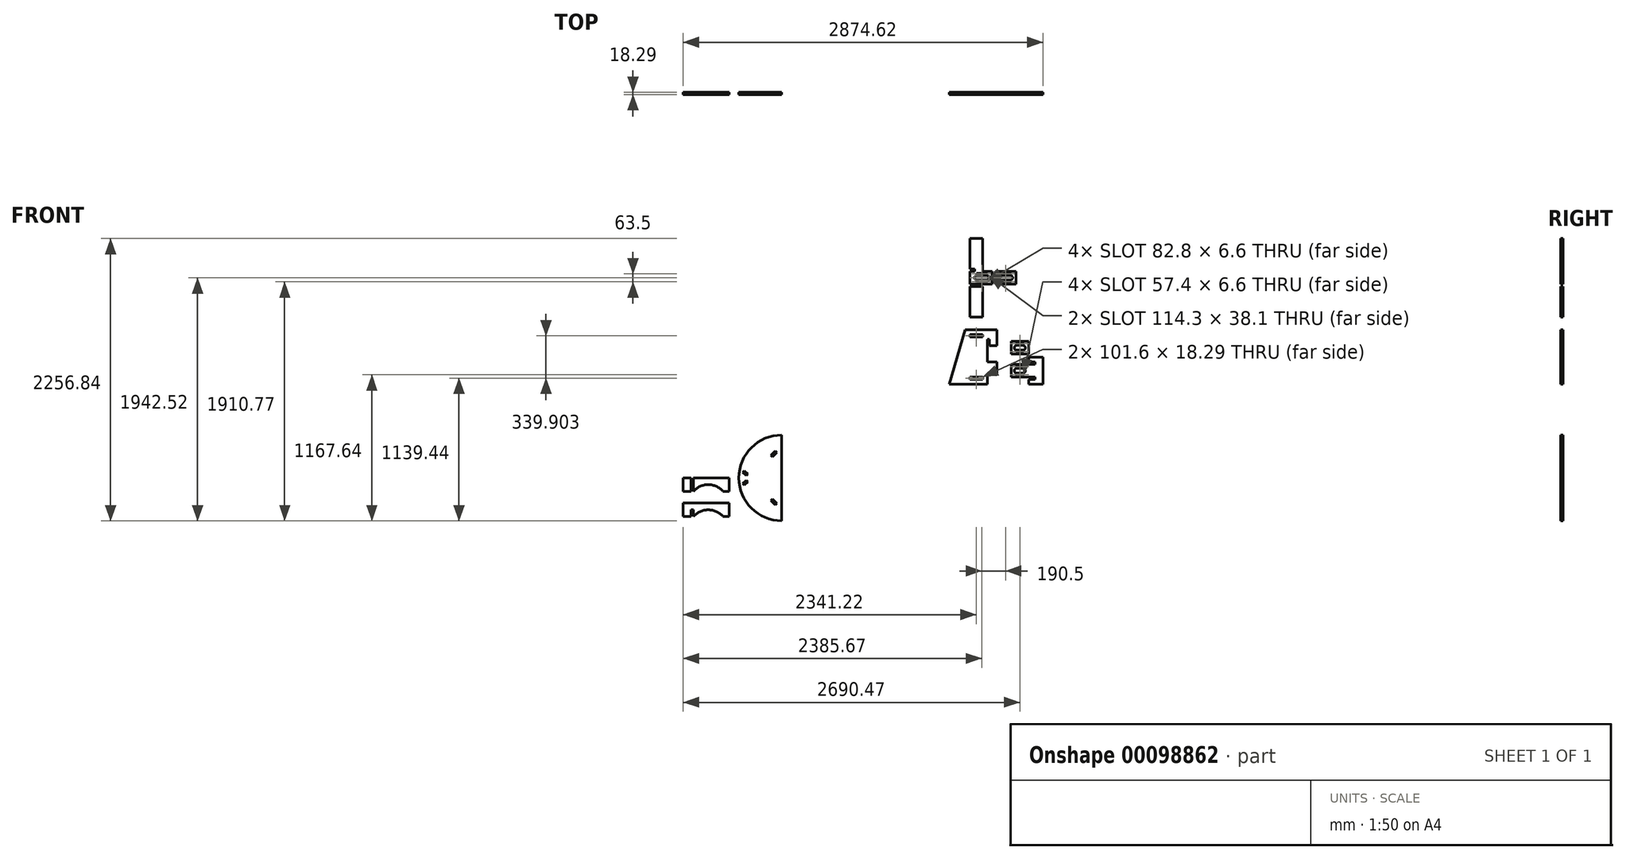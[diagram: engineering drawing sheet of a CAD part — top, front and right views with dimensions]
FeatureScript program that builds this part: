
annotation { "Feature Type Name" : "Feature", "Feature Type Description" : "" }
export const myFeature = defineFeature(function(context is Context, id is Id, definition is map)
    precondition{}
    {
        {
            var Q0;
            Q0=qCreatedBy(makeId("Front.planeOp"),FACE);
            var sketch = newSketch(context, id + "F0", { "sketchPlane" : qUnion([Q0])});
            skLineSegment(sketch, "E0.bottom", {"start": v(-889, 508) * mm, "end": v(889, 508) * mm, "construction": true});
            skLineSegment(sketch, "E0.top", {"start": v(-889, -508) * mm, "end": v(889, -508) * mm, "construction": true});
            skLineSegment(sketch, "E0.left", {"start": v(-889, 508) * mm, "end": v(-889, -508) * mm, "construction": true});
            skLineSegment(sketch, "E0.right", {"start": v(889, 508) * mm, "end": v(889, -508) * mm, "construction": true});
            skPoint(sketch, "E0.middle", {"position": v(0, 0) * mm});
            skArc(sketch, "E1", {"start": v(-889, 177.8) * mm, "mid": v(-1231.9, -165.1) * mm, "end": v(-889, -508) * mm, "construction": true});
            skLineSegment(sketch, "E2", {"start": v(0, -508) * mm, "end": v(0, 508) * mm, "construction": true});
            skArc(sketch, "E3", {"start": v(-1651, 177.8) * mm, "mid": v(-1993.9, -165.1) * mm, "end": v(-1651, -508) * mm});
            skLineSegment(sketch, "E4", {"start": v(-1651, 177.8) * mm, "end": v(-1651, -508) * mm});
            skPoint(sketch, "E5.startSnap0", {"position": v(-1993.9, -165.1) * mm});
            skLineSegment(sketch, "E6", {"start": v(-1689.1, 38.1) * mm, "end": v(-1689.1, -368.3) * mm});
            skLineSegment(sketch, "E7.0", {"start": v(-1981.97, -254.77) * mm, "end": v(-1689.1, 38.1) * mm, "construction": true});
            skLineSegment(sketch, "E8.0", {"start": v(-1981.97, -75.43) * mm, "end": v(-1689.1, -368.3) * mm, "construction": true});
            skLineSegment(sketch, "E9.0", {"start": v(-1986.93, -96.33) * mm, "end": v(-1689.1, -394.16) * mm, "construction": true});
            skLineSegment(sketch, "E10.0", {"start": v(-1986.93, -233.87) * mm, "end": v(-1689.1, 63.96) * mm, "construction": true});
            skPoint(sketch, "E11", {"position": v(-1918.16, -165.1) * mm});
            skLineSegment(sketch, "E12", {"start": v(-1993.9, -165.1) * mm, "end": v(-1651, -165.1) * mm, "construction": true});
            skPoint(sketch, "E13", {"position": v(-1689.1, -165.1) * mm});
            skLineSegment(sketch, "E14", {"start": v(-1963.06, -120.2) * mm, "end": v(-1950.13, -107.27) * mm});
            skLineSegment(sketch, "E15", {"start": v(-1936.12, -147.14) * mm, "end": v(-1923.2, -134.2) * mm});
            skLineSegment(sketch, "E16", {"start": v(-1689.1, -368.3) * mm, "end": v(-1702.03, -381.23) * mm});
            skLineSegment(sketch, "E17", {"start": v(-1725.02, -332.38) * mm, "end": v(-1737.95, -345.31) * mm});
            skLineSegment(sketch, "E18", {"start": v(-1950.13, -107.27) * mm, "end": v(-1923.2, -134.2) * mm});
            skLineSegment(sketch, "E19", {"start": v(-1936.12, -147.14) * mm, "end": v(-1963.06, -120.2) * mm});
            skLineSegment(sketch, "E20", {"start": v(-1737.95, -345.31) * mm, "end": v(-1702.03, -381.23) * mm});
            skLineSegment(sketch, "E21", {"start": v(-1725.02, -332.38) * mm, "end": v(-1689.1, -368.3) * mm});
            skLineSegment(sketch, "E22.MirrorCS", {"start": v(-1689.1, 38.1) * mm, "end": v(-1702.03, 51.03) * mm});
            skLineSegment(sketch, "E23.MirrorCS", {"start": v(-1725.02, 2.18) * mm, "end": v(-1737.95, 15.11) * mm});
            skLineSegment(sketch, "E24.MirrorCS", {"start": v(-1737.95, 15.11) * mm, "end": v(-1702.03, 51.03) * mm});
            skLineSegment(sketch, "E25.MirrorCS", {"start": v(-1725.02, 2.18) * mm, "end": v(-1689.1, 38.1) * mm});
            skLineSegment(sketch, "E26.MirrorCS", {"start": v(-1950.13, -222.93) * mm, "end": v(-1923.2, -196) * mm});
            skLineSegment(sketch, "E27.MirrorCS", {"start": v(-1936.12, -183.06) * mm, "end": v(-1963.06, -210) * mm});
            skLineSegment(sketch, "E28.MirrorCS", {"start": v(-1963.06, -210) * mm, "end": v(-1950.13, -222.93) * mm});
            skLineSegment(sketch, "E29.MirrorCS", {"start": v(-1936.12, -183.06) * mm, "end": v(-1923.2, -196) * mm});
            skLineSegment(sketch, "E30", {"start": v(-1950.13, -107.27) * mm, "end": v(-1689.1, -368.3) * mm});
            skLineSegment(sketch, "E31.bottom", {"start": v(-2439.26, -165.1) * mm, "end": v(-2070.1, -165.1) * mm});
            skLineSegment(sketch, "E31.top", {"start": v(-2439.26, -272.29) * mm, "end": v(-2070.1, -272.29) * mm});
            skLineSegment(sketch, "E31.left", {"start": v(-2439.26, -165.1) * mm, "end": v(-2439.26, -272.29) * mm});
            skLineSegment(sketch, "E31.right", {"start": v(-2070.1, -165.1) * mm, "end": v(-2070.1, -272.29) * mm});
            skLineSegment(sketch, "E32.bottom", {"start": v(-2070.1, -165.1) * mm, "end": v(-2120.9, -165.1) * mm});
            skLineSegment(sketch, "E32.top", {"start": v(-2070.1, -146.81) * mm, "end": v(-2120.9, -146.81) * mm});
            skLineSegment(sketch, "E32.left", {"start": v(-2070.1, -165.1) * mm, "end": v(-2070.1, -146.81) * mm});
            skLineSegment(sketch, "E32.right", {"start": v(-2120.9, -165.1) * mm, "end": v(-2120.9, -146.81) * mm});
            skLineSegment(sketch, "E33.bottom", {"start": v(-2439.26, -165.1) * mm, "end": v(-2401.16, -165.1) * mm});
            skLineSegment(sketch, "E33.top", {"start": v(-2439.26, -146.81) * mm, "end": v(-2401.16, -146.81) * mm});
            skLineSegment(sketch, "E33.left", {"start": v(-2439.26, -165.1) * mm, "end": v(-2439.26, -146.81) * mm});
            skLineSegment(sketch, "E33.right", {"start": v(-2401.16, -165.1) * mm, "end": v(-2401.16, -146.81) * mm});
            skPoint(sketch, "E34.oppositeSnap0", {"position": v(-2439.26, -218.7) * mm});
            skLineSegment(sketch, "E34.bottom", {"start": v(-2375.76, -272.29) * mm, "end": v(-2357.47, -272.29) * mm});
            skLineSegment(sketch, "E34.top", {"start": v(-2375.76, -218.7) * mm, "end": v(-2357.47, -218.7) * mm});
            skLineSegment(sketch, "E34.left", {"start": v(-2375.76, -272.29) * mm, "end": v(-2375.76, -218.7) * mm});
            skLineSegment(sketch, "E34.right", {"start": v(-2357.47, -272.29) * mm, "end": v(-2357.47, -218.7) * mm});
            skLineSegment(sketch, "E35.top", {"start": v(-2375.76, -165.1) * mm, "end": v(-2357.47, -165.1) * mm});
            skLineSegment(sketch, "E35.left", {"start": v(-2375.76, -218.7) * mm, "end": v(-2375.76, -165.1) * mm});
            skLineSegment(sketch, "E35.right", {"start": v(-2357.47, -218.7) * mm, "end": v(-2357.47, -165.1) * mm});
            skLineSegment(sketch, "E36.bottom", {"start": v(-2439.26, -366.78) * mm, "end": v(-2070.1, -366.78) * mm});
            skLineSegment(sketch, "E36.top", {"start": v(-2439.26, -473.96) * mm, "end": v(-2070.1, -473.96) * mm});
            skLineSegment(sketch, "E36.left", {"start": v(-2439.26, -366.78) * mm, "end": v(-2439.26, -473.96) * mm});
            skLineSegment(sketch, "E36.right", {"start": v(-2070.1, -366.78) * mm, "end": v(-2070.1, -473.96) * mm});
            skLineSegment(sketch, "E37.bottom", {"start": v(-2070.1, -366.78) * mm, "end": v(-2120.9, -366.78) * mm});
            skLineSegment(sketch, "E37.top", {"start": v(-2070.1, -348.49) * mm, "end": v(-2120.9, -348.49) * mm});
            skLineSegment(sketch, "E37.left", {"start": v(-2070.1, -366.78) * mm, "end": v(-2070.1, -348.49) * mm});
            skLineSegment(sketch, "E37.right", {"start": v(-2120.9, -366.78) * mm, "end": v(-2120.9, -348.49) * mm});
            skLineSegment(sketch, "E38.bottom", {"start": v(-2439.26, -366.78) * mm, "end": v(-2401.16, -366.78) * mm});
            skLineSegment(sketch, "E38.top", {"start": v(-2439.26, -348.49) * mm, "end": v(-2401.16, -348.49) * mm});
            skLineSegment(sketch, "E38.left", {"start": v(-2439.26, -366.78) * mm, "end": v(-2439.26, -348.49) * mm});
            skLineSegment(sketch, "E38.right", {"start": v(-2401.16, -366.78) * mm, "end": v(-2401.16, -348.49) * mm});
            skPoint(sketch, "E39.oppositeSnap0", {"position": v(-2439.26, -420.37) * mm});
            skLineSegment(sketch, "E39.bottom", {"start": v(-2375.76, -473.96) * mm, "end": v(-2357.47, -473.96) * mm});
            skLineSegment(sketch, "E39.top", {"start": v(-2375.76, -420.37) * mm, "end": v(-2357.47, -420.37) * mm});
            skLineSegment(sketch, "E39.left", {"start": v(-2375.76, -473.96) * mm, "end": v(-2375.76, -420.37) * mm});
            skLineSegment(sketch, "E39.right", {"start": v(-2357.47, -473.96) * mm, "end": v(-2357.47, -420.37) * mm});
            skLineSegment(sketch, "E40.top", {"start": v(-2375.76, -366.78) * mm, "end": v(-2357.47, -366.78) * mm});
            skLineSegment(sketch, "E40.left", {"start": v(-2375.76, -420.37) * mm, "end": v(-2375.76, -366.78) * mm});
            skLineSegment(sketch, "E40.right", {"start": v(-2357.47, -420.37) * mm, "end": v(-2357.47, -366.78) * mm});
            skArc(sketch, "E41", {"start": v(-2120.9, -272.29) * mm, "mid": v(-2239.18, -218.7) * mm, "end": v(-2357.47, -272.29) * mm});
            skLineSegment(sketch, "E42", {"start": v(-2357.47, -218.7) * mm, "end": v(-2070.1, -218.7) * mm, "construction": true});
            skLineSegment(sketch, "E43", {"start": v(-2357.47, -420.37) * mm, "end": v(-2070.1, -420.37) * mm, "construction": true});
            skArc(sketch, "E44", {"start": v(-2120.9, -473.96) * mm, "mid": v(-2239.18, -420.37) * mm, "end": v(-2357.47, -473.96) * mm});
            skLineSegment(sketch, "E45.bottom", {"start": v(9.14, 660.4) * mm, "end": v(-9.14, 660.4) * mm, "construction": true});
            skLineSegment(sketch, "E45.top", {"start": v(9.14, 838.2) * mm, "end": v(-9.14, 838.2) * mm, "construction": true});
            skLineSegment(sketch, "E45.left", {"start": v(9.14, 660.4) * mm, "end": v(9.14, 838.2) * mm, "construction": true});
            skLineSegment(sketch, "E45.right", {"start": v(-9.14, 660.4) * mm, "end": v(-9.14, 838.2) * mm, "construction": true});
            skPoint(sketch, "E45.middle", {"position": v(0, 749.3) * mm});
            skLineSegment(sketch, "E46.bottom", {"start": v(9.14, 942.4) * mm, "end": v(-9.14, 942.4) * mm});
            skLineSegment(sketch, "E46.top", {"start": v(9.14, 929.7) * mm, "end": v(-9.14, 929.7) * mm});
            skLineSegment(sketch, "E46.left", {"start": v(9.14, 942.4) * mm, "end": v(9.14, 929.7) * mm});
            skLineSegment(sketch, "E46.right", {"start": v(-9.14, 942.4) * mm, "end": v(-9.14, 929.7) * mm, "construction": true});
            skPoint(sketch, "E46.middle", {"position": v(0, 936.04) * mm});
            skLineSegment(sketch, "E47.bottom", {"start": v(-9.14, 660.4) * mm, "end": v(67.06, 660.4) * mm});
            skLineSegment(sketch, "E47.top", {"start": v(-9.14, 762) * mm, "end": v(67.06, 762) * mm});
            skLineSegment(sketch, "E47.left", {"start": v(-9.14, 660.4) * mm, "end": v(-9.14, 762) * mm});
            skLineSegment(sketch, "E47.right", {"start": v(67.06, 660.4) * mm, "end": v(67.06, 762) * mm});
            skLineSegment(sketch, "E48.bottom", {"start": v(67.06, 660.4) * mm, "end": v(9.14, 660.4) * mm});
            skLineSegment(sketch, "E48.top", {"start": v(67.06, 584.2) * mm, "end": v(9.14, 584.2) * mm});
            skLineSegment(sketch, "E48.left", {"start": v(67.06, 660.4) * mm, "end": v(67.06, 584.2) * mm});
            skLineSegment(sketch, "E48.right", {"start": v(9.14, 660.4) * mm, "end": v(9.14, 584.2) * mm});
            skLineSegment(sketch, "E49.bottom", {"start": v(-9.14, 929.7) * mm, "end": v(67.06, 929.7) * mm, "construction": true});
            skLineSegment(sketch, "E49.top", {"start": v(-9.14, 1018.6) * mm, "end": v(67.06, 1018.6) * mm});
            skLineSegment(sketch, "E49.left", {"start": v(-9.14, 929.7) * mm, "end": v(-9.14, 1018.6) * mm, "construction": true});
            skLineSegment(sketch, "E49.right", {"start": v(67.06, 929.7) * mm, "end": v(67.06, 1018.6) * mm});
            skLineSegment(sketch, "E50", {"start": v(-9.14, 1018.6) * mm, "end": v(-186.94, 1018.6) * mm});
            skLineSegment(sketch, "E51", {"start": v(-313.94, 584.2) * mm, "end": v(-186.94, 1018.6) * mm});
            skLineSegment(sketch, "E52", {"start": v(-9.14, 929.7) * mm, "end": v(-9.14, 762) * mm});
            skLineSegment(sketch, "E53", {"start": v(-9.14, 660.4) * mm, "end": v(-9.14, 584.2) * mm});
            skLineSegment(sketch, "E54", {"start": v(-9.14, 584.2) * mm, "end": v(-313.94, 584.2) * mm});
            skLineSegment(sketch, "E55", {"start": v(9.14, 929.7) * mm, "end": v(9.14, 891.6) * mm});
            skLineSegment(sketch, "E56", {"start": v(9.14, 891.6) * mm, "end": v(67.06, 891.6) * mm});
            skLineSegment(sketch, "E57", {"start": v(67.06, 891.6) * mm, "end": v(67.06, 929.7) * mm});
            skLineSegment(sketch, "E58.bottom", {"start": v(-148.84, 622.3) * mm, "end": v(-47.24, 622.3) * mm});
            skLineSegment(sketch, "E58.top", {"start": v(-148.84, 640.59) * mm, "end": v(-47.24, 640.59) * mm});
            skLineSegment(sketch, "E58.left", {"start": v(-148.84, 622.3) * mm, "end": v(-148.84, 640.59) * mm});
            skLineSegment(sketch, "E58.right", {"start": v(-47.24, 622.3) * mm, "end": v(-47.24, 640.59) * mm});
            skLineSegment(sketch, "E59.bottom", {"start": v(-148.84, 980.5) * mm, "end": v(-47.24, 980.5) * mm});
            skLineSegment(sketch, "E59.top", {"start": v(-148.84, 962.2) * mm, "end": v(-47.24, 962.2) * mm});
            skLineSegment(sketch, "E59.left", {"start": v(-148.84, 980.5) * mm, "end": v(-148.84, 962.2) * mm});
            skLineSegment(sketch, "E59.right", {"start": v(-47.24, 980.5) * mm, "end": v(-47.24, 962.2) * mm});
            skPoint(sketch, "E60", {"position": v(-161.54, 584.2) * mm});
            skLineSegment(sketch, "E61.bottom", {"start": v(-148.84, 1120.2) * mm, "end": v(-47.24, 1120.2) * mm});
            skLineSegment(sketch, "E61.top", {"start": v(-148.84, 1365.43) * mm, "end": v(-47.24, 1365.43) * mm});
            skLineSegment(sketch, "E61.left", {"start": v(-148.84, 1120.2) * mm, "end": v(-148.84, 1365.43) * mm});
            skLineSegment(sketch, "E61.right", {"start": v(-47.24, 1120.2) * mm, "end": v(-47.24, 1365.43) * mm});
            skPoint(sketch, "E62.oppositeSnap0", {"position": v(-98.04, 1365.43) * mm});
            skLineSegment(sketch, "E62.bottom", {"start": v(-47.24, 1365.43) * mm, "end": v(-98.04, 1365.43) * mm});
            skLineSegment(sketch, "E62.top", {"start": v(-47.24, 1383.72) * mm, "end": v(-98.04, 1383.72) * mm});
            skLineSegment(sketch, "E62.left", {"start": v(-47.24, 1365.43) * mm, "end": v(-47.24, 1383.72) * mm});
            skLineSegment(sketch, "E62.right", {"start": v(-98.04, 1365.43) * mm, "end": v(-98.04, 1383.72) * mm, "construction": true});
            skLineSegment(sketch, "E63", {"start": v(-148.84, 1485.32) * mm, "end": v(28.96, 1485.32) * mm});
            skLineSegment(sketch, "E64", {"start": v(28.96, 1383.72) * mm, "end": v(28.96, 1485.32) * mm});
            skLineSegment(sketch, "E65", {"start": v(-148.84, 1434.52) * mm, "end": v(28.96, 1434.52) * mm, "construction": true});
            skLineSegment(sketch, "E66.MirrorCS", {"start": v(-47.24, 1503.6) * mm, "end": v(-98.04, 1503.6) * mm});
            skLineSegment(sketch, "E67.MirrorCS", {"start": v(-47.24, 1748.84) * mm, "end": v(-47.24, 1503.6) * mm});
            skLineSegment(sketch, "E68.MirrorCS", {"start": v(-148.84, 1748.84) * mm, "end": v(-148.84, 1503.6) * mm});
            skLineSegment(sketch, "E69.MirrorCS", {"start": v(-148.84, 1503.6) * mm, "end": v(-47.24, 1503.6) * mm});
            skLineSegment(sketch, "E70.MirrorCS", {"start": v(-148.84, 1748.84) * mm, "end": v(-47.24, 1748.84) * mm});
            skLineSegment(sketch, "E71.MirrorCS", {"start": v(-98.04, 1503.6) * mm, "end": v(-98.04, 1485.32) * mm, "construction": true});
            skLineSegment(sketch, "E72.MirrorCS", {"start": v(-47.24, 1503.6) * mm, "end": v(-47.24, 1485.32) * mm});
            skPoint(sketch, "E73.MirrorP", {"position": v(-98.04, 1503.6) * mm});
            skLineSegment(sketch, "E74.MirrorCS", {"start": v(-47.24, 1485.32) * mm, "end": v(-98.04, 1485.32) * mm});
            skLineSegment(sketch, "E75", {"start": v(-9.14, 942.4) * mm, "end": v(-9.14, 929.7) * mm});
            skLineSegment(sketch, "E76", {"start": v(28.96, 1383.72) * mm, "end": v(-148.84, 1383.72) * mm});
            skLineSegment(sketch, "E77", {"start": v(-148.84, 1383.72) * mm, "end": v(-148.84, 1485.32) * mm});
            skLineSegment(sketch, "E78", {"start": v(-110.74, 1503.6) * mm, "end": v(-110.74, 1485.32) * mm});
            skLineSegment(sketch, "E79.MirrorCS", {"start": v(-110.74, 1365.43) * mm, "end": v(-110.74, 1383.72) * mm});
            skLineSegment(sketch, "E80.bottom", {"start": v(371.86, 622.3) * mm, "end": v(435.36, 622.3) * mm});
            skLineSegment(sketch, "E80.top", {"start": v(371.86, 640.59) * mm, "end": v(435.36, 640.59) * mm});
            skLineSegment(sketch, "E80.left", {"start": v(371.86, 622.3) * mm, "end": v(371.86, 640.59) * mm});
            skLineSegment(sketch, "E80.right", {"start": v(435.36, 622.3) * mm, "end": v(435.36, 640.59) * mm});
            skLineSegment(sketch, "E81.bottom", {"start": v(435.36, 622.3) * mm, "end": v(321.06, 622.3) * mm});
            skLineSegment(sketch, "E81.top", {"start": v(435.36, 584.2) * mm, "end": v(321.06, 584.2) * mm});
            skLineSegment(sketch, "E81.left", {"start": v(435.36, 622.3) * mm, "end": v(435.36, 584.2) * mm});
            skLineSegment(sketch, "E81.right", {"start": v(321.06, 622.3) * mm, "end": v(321.06, 584.2) * mm});
            skLineSegment(sketch, "E82.bottom", {"start": v(435.36, 640.59) * mm, "end": v(181.36, 640.59) * mm});
            skLineSegment(sketch, "E82.top", {"start": v(435.36, 742.19) * mm, "end": v(181.36, 742.19) * mm});
            skLineSegment(sketch, "E82.left", {"start": v(435.36, 640.59) * mm, "end": v(435.36, 742.19) * mm});
            skLineSegment(sketch, "E82.right", {"start": v(181.36, 640.59) * mm, "end": v(181.36, 742.19) * mm});
            skLineSegment(sketch, "E83", {"start": v(181.36, 691.39) * mm, "end": v(435.36, 691.39) * mm, "construction": true});
            skLineSegment(sketch, "E84.MirrorCS", {"start": v(371.86, 760.48) * mm, "end": v(371.86, 742.19) * mm});
            skLineSegment(sketch, "E85.MirrorCS", {"start": v(371.86, 760.48) * mm, "end": v(435.36, 760.48) * mm});
            skLineSegment(sketch, "E86.MirrorCS", {"start": v(371.86, 742.19) * mm, "end": v(435.36, 742.19) * mm});
            skLineSegment(sketch, "E87.MirrorCS", {"start": v(321.06, 760.48) * mm, "end": v(321.06, 798.58) * mm});
            skLineSegment(sketch, "E88.MirrorCS", {"start": v(435.36, 798.58) * mm, "end": v(321.06, 798.58) * mm});
            skLineSegment(sketch, "E89.MirrorCS", {"start": v(435.36, 760.48) * mm, "end": v(435.36, 798.58) * mm});
            skLineSegment(sketch, "E90.MirrorCS", {"start": v(435.36, 760.48) * mm, "end": v(435.36, 742.19) * mm});
            skLineSegment(sketch, "E91.MirrorCS", {"start": v(435.36, 760.48) * mm, "end": v(321.06, 760.48) * mm});
            skLineSegment(sketch, "E92", {"start": v(-15.5, 1434.52) * mm, "end": v(-91.7, 1434.52) * mm, "construction": true});
            skArc(sketch, "E93.0.startCap", {"start": v(-15.5, 1453.57) * mm, "mid": v(3.56, 1434.52) * mm, "end": v(-15.5, 1415.47) * mm});
            skArc(sketch, "E93.0.endCap", {"start": v(-91.7, 1415.47) * mm, "mid": v(-110.74, 1434.52) * mm, "end": v(-91.7, 1453.57) * mm});
            skLineSegment(sketch, "E93.0.left", {"start": v(-15.5, 1415.47) * mm, "end": v(-91.7, 1415.47) * mm});
            skLineSegment(sketch, "E93.0.right", {"start": v(-15.5, 1453.57) * mm, "end": v(-91.7, 1453.57) * mm});
            skLineSegment(sketch, "E94", {"start": v(225.8, 691.39) * mm, "end": v(276.6, 691.39) * mm, "construction": true});
            skArc(sketch, "E95.0.startCap", {"start": v(225.8, 672.34) * mm, "mid": v(206.76, 691.39) * mm, "end": v(225.8, 710.44) * mm});
            skArc(sketch, "E95.0.endCap", {"start": v(276.6, 710.44) * mm, "mid": v(295.66, 691.39) * mm, "end": v(276.6, 672.34) * mm});
            skLineSegment(sketch, "E95.0.left", {"start": v(225.8, 710.44) * mm, "end": v(276.6, 710.44) * mm});
            skLineSegment(sketch, "E95.0.right", {"start": v(225.8, 672.34) * mm, "end": v(276.6, 672.34) * mm});
            skLineSegment(sketch, "E96", {"start": v(-91.7, 1466.27) * mm, "end": v(-15.5, 1466.27) * mm, "construction": true});
            skArc(sketch, "E97.0.startCap", {"start": v(-91.7, 1462.96) * mm, "mid": v(-95, 1466.27) * mm, "end": v(-91.7, 1469.57) * mm});
            skArc(sketch, "E97.0.endCap", {"start": v(-15.5, 1469.57) * mm, "mid": v(-12.2, 1466.27) * mm, "end": v(-15.5, 1462.96) * mm});
            skLineSegment(sketch, "E97.0.left", {"start": v(-91.7, 1469.57) * mm, "end": v(-15.5, 1469.57) * mm});
            skLineSegment(sketch, "E97.0.right", {"start": v(-91.7, 1462.96) * mm, "end": v(-15.5, 1462.96) * mm});
            skLineSegment(sketch, "E98.MirrorCS", {"start": v(-91.7, 1406.07) * mm, "end": v(-15.5, 1406.07) * mm});
            skLineSegment(sketch, "E99.MirrorCS", {"start": v(-91.7, 1399.46) * mm, "end": v(-15.5, 1399.46) * mm});
            skArc(sketch, "E100.MirrorCS", {"start": v(-15.5, 1399.46) * mm, "mid": v(-12.2, 1402.77) * mm, "end": v(-15.5, 1406.07) * mm});
            skArc(sketch, "E101.MirrorCS", {"start": v(-91.7, 1406.07) * mm, "mid": v(-95, 1402.77) * mm, "end": v(-91.7, 1399.46) * mm});
            skLineSegment(sketch, "E102.MirrorCS", {"start": v(-91.7, 1402.77) * mm, "end": v(-15.5, 1402.77) * mm, "construction": true});
            skLineSegment(sketch, "E103", {"start": v(276.6, 723.14) * mm, "end": v(225.8, 723.14) * mm, "construction": true});
            skArc(sketch, "E104.0.startCap", {"start": v(276.6, 726.44) * mm, "mid": v(279.9, 723.14) * mm, "end": v(276.6, 719.84) * mm});
            skArc(sketch, "E104.0.endCap", {"start": v(225.8, 719.84) * mm, "mid": v(222.5, 723.14) * mm, "end": v(225.8, 726.44) * mm});
            skLineSegment(sketch, "E104.0.left", {"start": v(276.6, 719.84) * mm, "end": v(225.8, 719.84) * mm});
            skLineSegment(sketch, "E104.0.right", {"start": v(276.6, 726.44) * mm, "end": v(225.8, 726.44) * mm});
            skLineSegment(sketch, "E105.MirrorCS", {"start": v(276.6, 656.34) * mm, "end": v(225.8, 656.34) * mm});
            skArc(sketch, "E106.MirrorCS", {"start": v(225.8, 662.94) * mm, "mid": v(222.5, 659.64) * mm, "end": v(225.8, 656.34) * mm});
            skLineSegment(sketch, "E107.MirrorCS", {"start": v(276.6, 662.94) * mm, "end": v(225.8, 662.94) * mm});
            skArc(sketch, "E108.MirrorCS", {"start": v(276.6, 656.34) * mm, "mid": v(279.9, 659.64) * mm, "end": v(276.6, 662.94) * mm});
            skLineSegment(sketch, "E109.bottom", {"start": v(181.36, 823.98) * mm, "end": v(321.06, 823.98) * mm});
            skLineSegment(sketch, "E109.top", {"start": v(181.36, 925.58) * mm, "end": v(321.06, 925.58) * mm});
            skLineSegment(sketch, "E109.left", {"start": v(181.36, 823.98) * mm, "end": v(181.36, 925.58) * mm});
            skLineSegment(sketch, "E109.right", {"start": v(321.06, 823.98) * mm, "end": v(321.06, 925.58) * mm});
            skLineSegment(sketch, "E110", {"start": v(251.2, 823.98) * mm, "end": v(251.2, 742.19) * mm, "construction": true});
            skLineSegment(sketch, "E111", {"start": v(196.55, 783.08) * mm, "end": v(295.94, 783.08) * mm, "construction": true});
            skPoint(sketch, "E111.startSnap0", {"position": v(251.2, 783.08) * mm});
            skPoint(sketch, "E111.endSnap0", {"position": v(251.2, 783.08) * mm});
            skArc(sketch, "E112.MirrorCS", {"start": v(225.8, 903.22) * mm, "mid": v(222.5, 906.53) * mm, "end": v(225.8, 909.83) * mm});
            skArc(sketch, "E113.MirrorCS", {"start": v(276.6, 839.72) * mm, "mid": v(279.9, 843.03) * mm, "end": v(276.6, 846.33) * mm});
            skArc(sketch, "E114.MirrorCS", {"start": v(276.6, 909.83) * mm, "mid": v(279.9, 906.53) * mm, "end": v(276.6, 903.22) * mm});
            skArc(sketch, "E115.MirrorCS", {"start": v(225.8, 846.33) * mm, "mid": v(222.5, 843.03) * mm, "end": v(225.8, 839.72) * mm});
            skLineSegment(sketch, "E116.MirrorCS", {"start": v(225.8, 874.78) * mm, "end": v(276.6, 874.78) * mm, "construction": true});
            skLineSegment(sketch, "E117.MirrorCS", {"start": v(276.6, 843.03) * mm, "end": v(225.8, 843.03) * mm, "construction": true});
            skLineSegment(sketch, "E118.MirrorCS", {"start": v(276.6, 903.22) * mm, "end": v(225.8, 903.22) * mm});
            skLineSegment(sketch, "E119.MirrorCS", {"start": v(225.8, 855.73) * mm, "end": v(276.6, 855.73) * mm});
            skLineSegment(sketch, "E120.MirrorCS", {"start": v(276.6, 846.33) * mm, "end": v(225.8, 846.33) * mm});
            skLineSegment(sketch, "E121.MirrorCS", {"start": v(276.6, 839.72) * mm, "end": v(225.8, 839.72) * mm});
            skArc(sketch, "E122.MirrorCS", {"start": v(276.6, 855.73) * mm, "mid": v(295.66, 874.78) * mm, "end": v(276.6, 893.83) * mm});
            skLineSegment(sketch, "E123.MirrorCS", {"start": v(225.8, 893.83) * mm, "end": v(276.6, 893.83) * mm});
            skArc(sketch, "E124.MirrorCS", {"start": v(225.8, 893.83) * mm, "mid": v(206.76, 874.78) * mm, "end": v(225.8, 855.73) * mm});
            skLineSegment(sketch, "E125.MirrorCS", {"start": v(276.6, 909.83) * mm, "end": v(225.8, 909.83) * mm});
            skLineSegment(sketch, "E126.bottom", {"start": v(54.36, 1485.32) * mm, "end": v(219.46, 1485.32) * mm});
            skLineSegment(sketch, "E126.top", {"start": v(54.36, 1383.72) * mm, "end": v(219.46, 1383.72) * mm});
            skLineSegment(sketch, "E126.left", {"start": v(54.36, 1485.32) * mm, "end": v(54.36, 1383.72) * mm});
            skLineSegment(sketch, "E126.right", {"start": v(219.46, 1485.32) * mm, "end": v(219.46, 1383.72) * mm});
            skLineSegment(sketch, "E127", {"start": v(28.96, 1485.32) * mm, "end": v(54.36, 1485.32) * mm, "construction": true});
            skLineSegment(sketch, "E128", {"start": v(41.66, 1485.32) * mm, "end": v(41.66, 1383.72) * mm, "construction": true});
            skArc(sketch, "E129.MirrorCS", {"start": v(175, 1406.07) * mm, "mid": v(178.3, 1402.77) * mm, "end": v(175, 1399.46) * mm});
            skArc(sketch, "E130.MirrorCS", {"start": v(175, 1462.96) * mm, "mid": v(178.3, 1466.27) * mm, "end": v(175, 1469.57) * mm});
            skArc(sketch, "E131.MirrorCS", {"start": v(98.8, 1469.57) * mm, "mid": v(95.5, 1466.27) * mm, "end": v(98.8, 1462.96) * mm});
            skLineSegment(sketch, "E132.MirrorCS", {"start": v(98.8, 1415.47) * mm, "end": v(175, 1415.47) * mm});
            skLineSegment(sketch, "E133.MirrorCS", {"start": v(175, 1402.77) * mm, "end": v(98.8, 1402.77) * mm, "construction": true});
            skArc(sketch, "E134.MirrorCS", {"start": v(175, 1415.47) * mm, "mid": v(194.06, 1434.52) * mm, "end": v(175, 1453.57) * mm});
            skLineSegment(sketch, "E135.MirrorCS", {"start": v(175, 1466.27) * mm, "end": v(98.8, 1466.27) * mm, "construction": true});
            skLineSegment(sketch, "E136.MirrorCS", {"start": v(98.8, 1434.52) * mm, "end": v(175, 1434.52) * mm, "construction": true});
            skLineSegment(sketch, "E137.MirrorCS", {"start": v(175, 1399.46) * mm, "end": v(98.8, 1399.46) * mm});
            skLineSegment(sketch, "E138.MirrorCS", {"start": v(98.8, 1453.57) * mm, "end": v(175, 1453.57) * mm});
            skArc(sketch, "E139.MirrorCS", {"start": v(98.8, 1453.57) * mm, "mid": v(79.76, 1434.52) * mm, "end": v(98.8, 1415.47) * mm});
            skArc(sketch, "E140.MirrorCS", {"start": v(98.8, 1399.46) * mm, "mid": v(95.5, 1402.77) * mm, "end": v(98.8, 1406.07) * mm});
            skLineSegment(sketch, "E141.MirrorCS", {"start": v(175, 1406.07) * mm, "end": v(98.8, 1406.07) * mm});
            skLineSegment(sketch, "E142.MirrorCS", {"start": v(175, 1462.96) * mm, "end": v(98.8, 1462.96) * mm});
            skLineSegment(sketch, "E143.MirrorCS", {"start": v(175, 1469.57) * mm, "end": v(98.8, 1469.57) * mm});
            skSolve(sketch);
        }
        {
            var Q0;
            Q0=makeQuery(id+"F0.imprint","IMPRINT",FACE,{"disambiguationData":[TD([[makeQuery(id+"F0.imprint","IMPRINT",EDGE,{"derivedFrom":sQuery(id+"F0.wireOp",EDGE,"E33.bottom")}),1.0]])]});
            var Q1;
            {var subQ1=sQuery(id+"F0.wireOp",EDGE,"E31.left");Q1=makeQuery(id+"F0.imprint","IMPRINT",FACE,{"disambiguationData":[TD([[makeQuery(id+"F0.imprint","IMPRINT",EDGE,{"derivedFrom":subQ1}),1.0]])]});}
            var Q2;
            {var subQ1=sQuery(id+"F0.wireOp",EDGE,"E31.right");Q2=makeQuery(id+"F0.imprint","IMPRINT",FACE,{"disambiguationData":[TD([[makeQuery(id+"F0.imprint","IMPRINT",EDGE,{"derivedFrom":subQ1}),-1.0]])]});}
            var Q3;
            Q3=makeQuery(id+"F0.imprint","IMPRINT",FACE,{"disambiguationData":[TD([[makeQuery(id+"F0.imprint","IMPRINT",EDGE,{"derivedFrom":sQuery(id+"F0.wireOp",EDGE,"E32.bottom")}),-1.0]])]});
            var Q4;
            Q4=makeQuery(id+"F0.imprint","IMPRINT",FACE,{"disambiguationData":[TD([[makeQuery(id+"F0.imprint","IMPRINT",EDGE,{"derivedFrom":sQuery(id+"F0.wireOp",EDGE,"E3")}),1.0]])]});
            var Q5;
            Q5=makeQuery(id+"F0.imprint","IMPRINT",FACE,{"disambiguationData":[TD([[makeQuery(id+"F0.imprint","IMPRINT",EDGE,{"derivedFrom":sQuery(id+"F0.wireOp",EDGE,"E38.bottom")}),1.0]])]});
            var Q6;
            {var subQ1=sQuery(id+"F0.wireOp",EDGE,"E36.right");Q6=makeQuery(id+"F0.imprint","IMPRINT",FACE,{"disambiguationData":[TD([[makeQuery(id+"F0.imprint","IMPRINT",EDGE,{"derivedFrom":subQ1}),-1.0]])]});}
            var Q7;
            Q7=makeQuery(id+"F0.imprint","IMPRINT",FACE,{"disambiguationData":[TD([[makeQuery(id+"F0.imprint","IMPRINT",EDGE,{"derivedFrom":sQuery(id+"F0.wireOp",EDGE,"E37.bottom")}),-1.0]])]});
            var Q8;
            {var subQ1=sQuery(id+"F0.wireOp",EDGE,"E67.MirrorCS");Q8=makeQuery(id+"F0.imprint","IMPRINT",FACE,{"disambiguationData":[TD([[makeQuery(id+"F0.imprint","IMPRINT",EDGE,{"derivedFrom":subQ1}),-1.0]])]});}
            var Q9;
            {var subQ2=sQuery(id+"F0.wireOp",EDGE,"E71.MirrorCS");Q9=makeQuery(id+"F0.imprint","IMPRINT",FACE,{"disambiguationData":[TD([[makeQuery(id+"F0.imprint","IMPRINT",EDGE,{"derivedFrom":subQ2}),1.0]])]});}
            var Q10;
            {var subQ2=sQuery(id+"F0.wireOp",EDGE,"xodcvRnZ-B1O5-PV50-Xgqz-UQwxEgG8jyWU.right");Q10=makeQuery(id+"F0.imprint","IMPRINT",FACE,{"disambiguationData":[TD([[makeQuery(id+"F0.imprint","IMPRINT",EDGE,{"derivedFrom":subQ2}),-1.0]])]});}
            var Q11;
            Q11=makeQuery(id+"F0.imprint","IMPRINT",FACE,{"disambiguationData":[TD([[makeQuery(id+"F0.imprint","IMPRINT",EDGE,{"derivedFrom":sQuery(id+"F0.wireOp",EDGE,"E46.bottom")}),-1.0]])]});
            var Q12;
            Q12=makeQuery(id+"F0.imprint","IMPRINT",FACE,{"disambiguationData":[TD([[makeQuery(id+"F0.imprint","IMPRINT",EDGE,{"derivedFrom":sQuery(id+"F0.wireOp",EDGE,"E47.bottom")}),1.0]])]});
            var Q13;
            Q13=makeQuery(id+"F0.imprint","IMPRINT",FACE,{"disambiguationData":[TD([[makeQuery(id+"F0.imprint","IMPRINT",EDGE,{"derivedFrom":sQuery(id+"F0.wireOp",EDGE,"E48.bottom")}),1.0]])]});
            var Q14;
            {var subQ1=sQuery(id+"F0.wireOp",EDGE,"E64");Q14=makeQuery(id+"F0.imprint","IMPRINT",FACE,{"disambiguationData":[TD([[makeQuery(id+"F0.imprint","IMPRINT",EDGE,{"derivedFrom":subQ1}),1.0]])]});}
            var Q15;
            {var subQ0=sQuery(id+"F0.wireOp",EDGE,"E72.MirrorCS");Q15=makeQuery(id+"F0.imprint","IMPRINT",FACE,{"disambiguationData":[TD([[makeQuery(id+"F0.imprint","IMPRINT",EDGE,{"derivedFrom":subQ0}),-1.0]])]});}
            var Q16;
            {var subQ3=sQuery(id+"F0.wireOp",EDGE,"E87.MirrorCS");Q16=makeQuery(id+"F0.imprint","IMPRINT",FACE,{"disambiguationData":[TD([[makeQuery(id+"F0.imprint","IMPRINT",EDGE,{"derivedFrom":subQ3}),-1.0]])]});}
            var Q17;
            {var subQ0=sQuery(id+"F0.wireOp",EDGE,"E84.MirrorCS");Q17=makeQuery(id+"F0.imprint","IMPRINT",FACE,{"disambiguationData":[TD([[makeQuery(id+"F0.imprint","IMPRINT",EDGE,{"derivedFrom":subQ0}),1.0]])]});}
            var Q18;
            Q18=makeQuery(id+"F0.imprint","IMPRINT",FACE,{"disambiguationData":[TD([[makeQuery(id+"F0.imprint","IMPRINT",EDGE,{"derivedFrom":sQuery(id+"F0.wireOp",EDGE,"E82.top")}),1.0]])]});
            var Q19;
            {var subQ0=sQuery(id+"F0.wireOp",EDGE,"E80.left");Q19=makeQuery(id+"F0.imprint","IMPRINT",FACE,{"disambiguationData":[TD([[makeQuery(id+"F0.imprint","IMPRINT",EDGE,{"derivedFrom":subQ0}),-1.0]])]});}
            var Q20;
            Q20=makeQuery(id+"F0.imprint","IMPRINT",FACE,{"disambiguationData":[TD([[makeQuery(id+"F0.imprint","IMPRINT",EDGE,{"derivedFrom":sQuery(id+"F0.wireOp",EDGE,"E81.top")}),-1.0]])]});
            var Q21;
            {var subQ3=sQuery(id+"F0.wireOp",EDGE,"E62.bottom");Q21=makeQuery(id+"F0.imprint","IMPRINT",FACE,{"disambiguationData":[TD([[makeQuery(id+"F0.imprint","IMPRINT",EDGE,{"derivedFrom":subQ3}),-1.0]])]});}
            var Q22;
            {var subQ1=sQuery(id+"F0.wireOp",EDGE,"E36.left");Q22=makeQuery(id+"F0.imprint","IMPRINT",FACE,{"disambiguationData":[TD([[makeQuery(id+"F0.imprint","IMPRINT",EDGE,{"derivedFrom":subQ1}),1.0]])]});}
            var Q23;
            Q23=makeQuery(id+"F0.imprint","IMPRINT",FACE,{"disambiguationData":[TD([[makeQuery(id+"F0.imprint","IMPRINT",EDGE,{"derivedFrom":sQuery(id+"F0.wireOp",EDGE,"E39.top")}),1.0]])]});
            var Q24;
            Q24=makeQuery(id+"F0.imprint","IMPRINT",FACE,{"disambiguationData":[TD([[makeQuery(id+"F0.imprint","IMPRINT",EDGE,{"derivedFrom":sQuery(id+"F0.wireOp",EDGE,"E34.bottom")}),1.0]])]});
            var Q25;
            Q25=makeQuery(id+"F0.imprint","IMPRINT",FACE,{"disambiguationData":[TD([[makeQuery(id+"F0.imprint","IMPRINT",EDGE,{"derivedFrom":sQuery(id+"F0.wireOp",EDGE,"Em3j2uNX-hVYB-NjGB-Z9oH-VulC7OeTEeeO.bottom")}),-1.0]])]});
            var Q26;
            {var subQ0=sQuery(id+"F0.wireOp",EDGE,"E61.right");Q26=makeQuery(id+"F0.imprint","IMPRINT",FACE,{"disambiguationData":[TD([[makeQuery(id+"F0.imprint","IMPRINT",EDGE,{"derivedFrom":subQ0}),1.0]])]});}
            var Q27;
            Q27=makeQuery(id+"F0.imprint","IMPRINT",FACE,{"disambiguationData":[TD([[makeQuery(id+"F0.imprint","IMPRINT",EDGE,{"derivedFrom":sQuery(id+"F0.wireOp",EDGE,"E109.bottom")}),1.0]])]});
            var Q28;
            Q28=makeQuery(id+"F0.imprint","IMPRINT",FACE,{"disambiguationData":[TD([[makeQuery(id+"F0.imprint","IMPRINT",EDGE,{"derivedFrom":sQuery(id+"F0.wireOp",EDGE,"E126.bottom")}),-1.0]])]});
            extrude(context, id + "F1", {"entities" : qUnion([Q0, Q1, Q2, Q3, Q4, Q5, Q6, Q7, Q8, Q9, Q10, Q11, Q12, Q13, Q14, Q15, Q16, Q17, Q18, Q19, Q20, Q21, Q22, Q23, Q24, Q25, Q26, Q27, Q28]), "depth" : 18.29 * mm});
        }
    });
